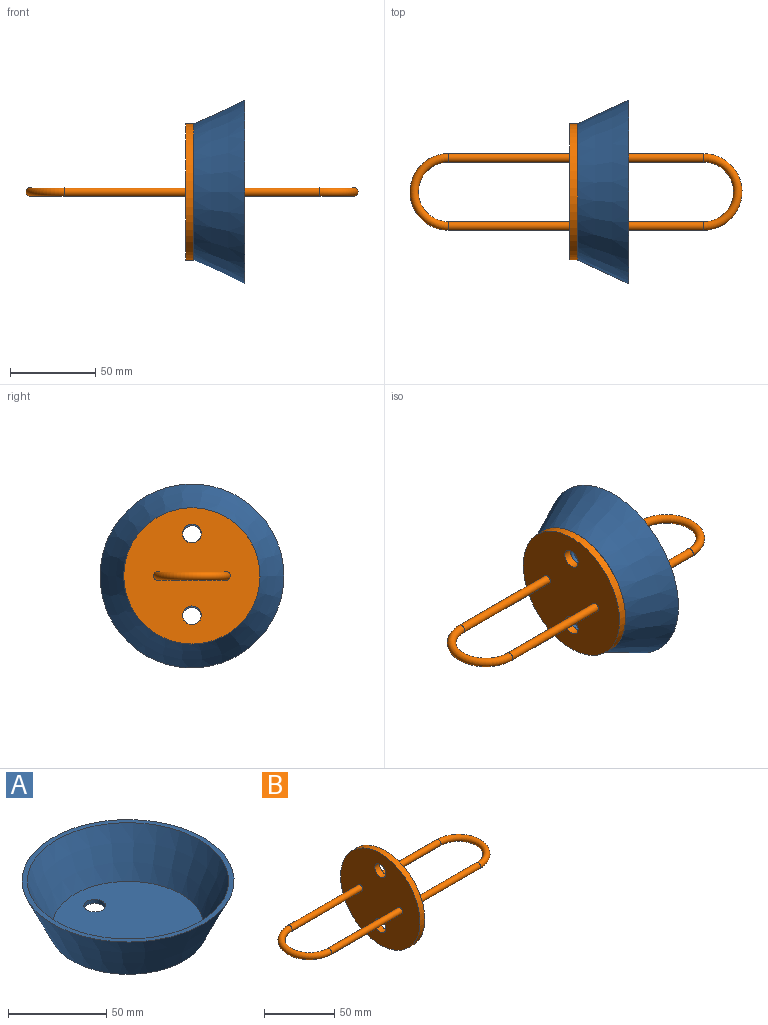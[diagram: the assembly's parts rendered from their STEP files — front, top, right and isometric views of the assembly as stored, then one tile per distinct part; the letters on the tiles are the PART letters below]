
ASSEMBLY  parts=2 mates=1
PART A: 7 faces, bbox 108x108x30 mm
  f0: cone r=40mm half-angle=25deg, axis (0,0,1), area 9774mm2, adj f1,f2
  f1: plane 107.98x107.98mm, normal (0,0,1), area 911.8mm2, adj f0,f3
  f2: plane 80x80mm, normal (0,0,-1), area 4836.5mm2, adj f0,f5,f6
  f3: cone r=37.73mm half-angle=25deg, axis (0,0,1), area 8544.8mm2, adj f1,f4
  f4: plane 76.81x76.81mm, normal (0,0,1), area 4444.2mm2, adj f3,f5,f6
  f5: cylinder r=5.5mm len=11mm, axis (0,0,1), area 86.4mm2, adj f2,f4
  f6: cylinder r=5.5mm len=11mm, axis (0,0,1), area 86.4mm2, adj f2,f4
PART B: 11 faces, bbox 198.7x80x80 mm
  f0: cylinder r=2.5mm len=73.88mm, axis (-1,0,0), area 1160.5mm2, adj f1,f4
  f1: torus R=20mm, axis (0,0,1), area 987mm2, adj f0,f2
  f2: cylinder r=2.5mm len=73.88mm, axis (1,0,0), area 1160.5mm2, adj f1,f4
  f3: cylinder r=40mm len=80mm, axis (-1,0,0), area 1231.5mm2, adj f4,f5
  f4: plane 80x80mm, normal (1,0,0), area 4797.2mm2, adj f0,f2,f3,f9,f10
  f5: plane 80x80mm, normal (-1,0,0), area 4797.2mm2, adj f3,f6,f8,f9,f10
  f6: cylinder r=2.5mm len=71.22mm, axis (-1,0,0), area 1118.8mm2, adj f5,f7
  f7: torus R=20mm, axis (0,0,1), area 987mm2, adj f6,f8
  f8: cylinder r=2.5mm len=71.22mm, axis (1,0,0), area 1118.8mm2, adj f5,f7
  f9: cylinder r=5.5mm len=11mm, axis (-1,0,0), area 169.3mm2, adj f4,f5
  f10: cylinder r=5.5mm len=11mm, axis (-1,0,0), area 169.3mm2, adj f4,f5
PLACE A rot(axis=(-0.58,0.58,-0.58),120deg) t=(-28.98,2.58,29.91)mm
PLACE B t=(-31.43,-17.42,29.94)mm fixed
MATE fastened A.f0 <-> B.f4  axis (-1,0,0) through (-28.98,2.58,29.91)mm
